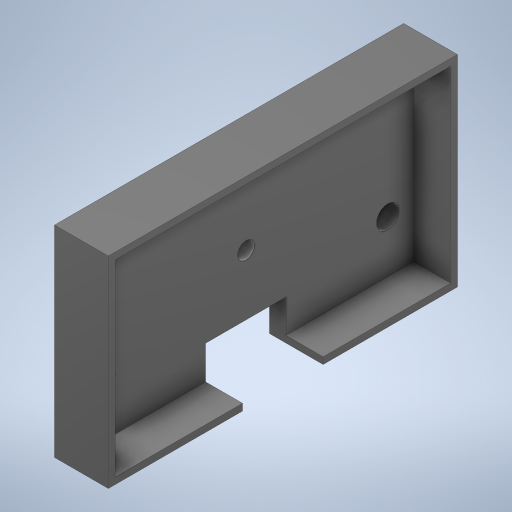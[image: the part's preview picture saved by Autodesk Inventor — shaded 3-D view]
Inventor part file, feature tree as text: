
AUTODESK INVENTOR PART (.ipt)
format: ipt  version: 2023 (Build 270158000, 158)  size: 261,120 bytes
history: native  units: mm
features: sketch x5, extrude x3, hole x2
ambient origin geometry x8: Origin, YZ Plane, XZ Plane, XY Plane, X Axis, Y Axis, Z Axis, Center Point
bodies: Volumenkörper1 (feature_tree)
feature tree (10):
  extrude  "Extrusion1"  Depth=52.0mm
  extrude  "Extrusion2"  Depth=50.0mm
  extrude  "Extrusion3"  Depth=5.5mm TaperAngle=0.0deg
  hole  "Bohrung1"  [1 undecoded]
  hole  "Bohrung3"  [1 undecoded]
  sketch  "Skizze1"  dims[d0=30.0mm d1=52.0mm]
  sketch  "Skizze2"  dims[d2=8.0mm d3=0.0mm d4=50.0mm]
  sketch  "Skizze3"  dims[d5=28.0mm d6=5.5mm d7=0.0mm]
  sketch  "Skizze4"  dims[d8=12.0mm d9=6.0mm]
  sketch  "Skizze7"  dims[d10=6.0mm d11=0.0mm d12=0.0mm d13=3.4mm d14=6.0mm d15=4.0mm d16=2.0mm d17=90.0deg d18=8.0mm d19=20.594885mm d20=17.25mm d21=17.25mm d22=11.0mm d23=11.0mm d24=42.25mm d25=42.25mm d26=21.125mm d27=21.125mm d44=2.5mm d45=6.0mm d46=4.0mm d47=2.0mm d48=90.0deg d49=8.0mm d50=20.594885mm d51=0.0mm d52=0.0mm]
note: 2 required parameter values undecoded (feature->parameter linkage not recoverable at this tier; creation-order binding heuristic only, values carry confidence <= 0.55)
